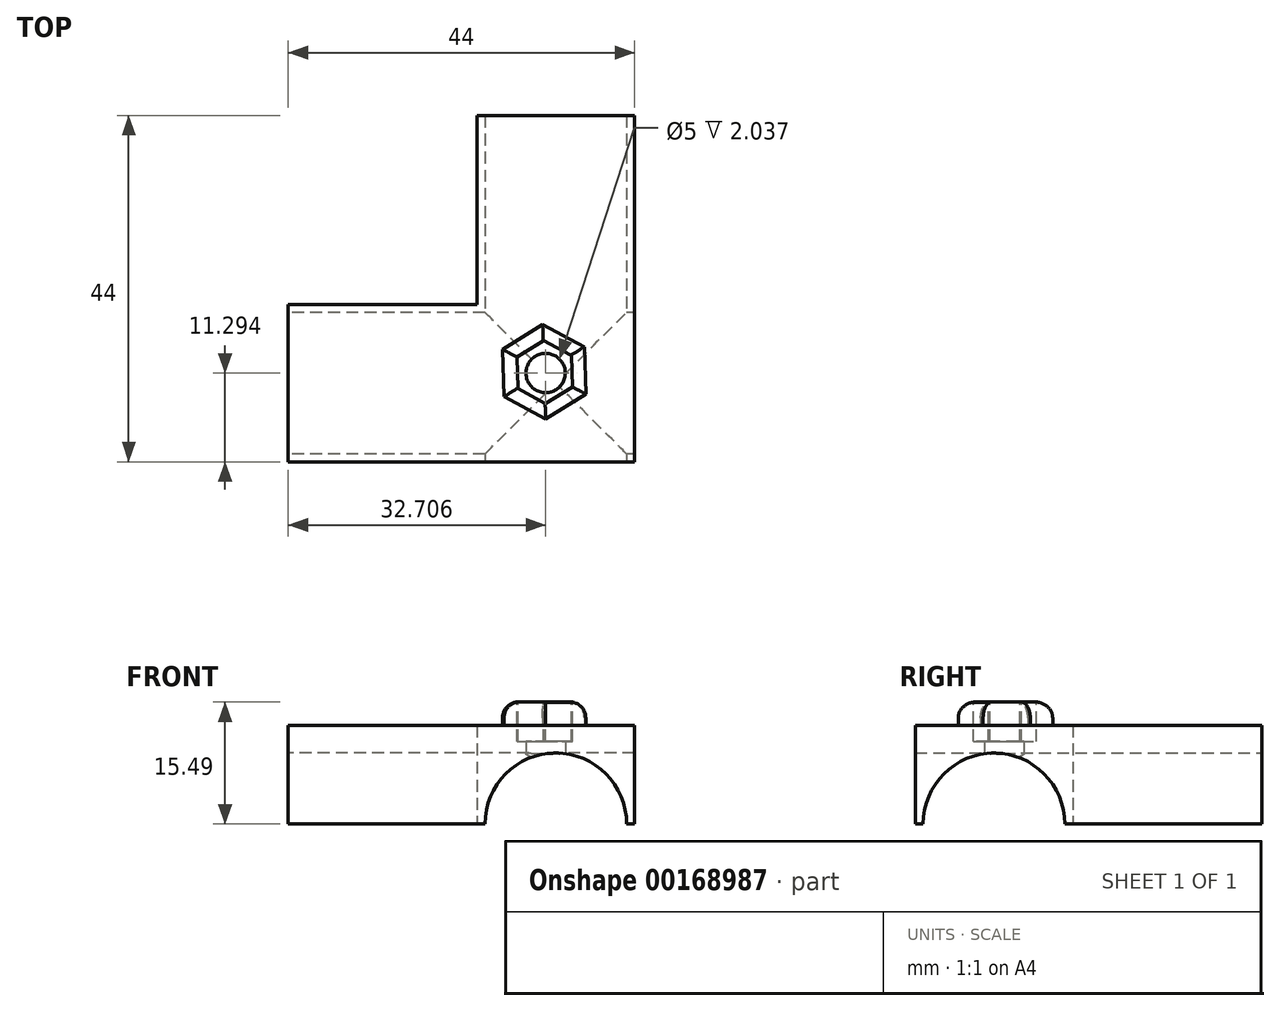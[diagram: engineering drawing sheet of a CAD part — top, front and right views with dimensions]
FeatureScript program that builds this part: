
annotation { "Feature Type Name" : "Feature", "Feature Type Description" : "" }
export const myFeature = defineFeature(function(context is Context, id is Id, definition is map)
    precondition{}
    {
        {
            var Q0;
            Q0=qCreatedBy(makeId("Top.planeOp"),FACE);
            var sketch = newSketch(context, id + "F0", { "sketchPlane" : qUnion([Q0])});
            skLineSegment(sketch, "E0", {"start": v(0, 24) * mm, "end": v(20, 24) * mm});
            skLineSegment(sketch, "E1", {"start": v(20, 24) * mm, "end": v(20, -20) * mm});
            skLineSegment(sketch, "E2", {"start": v(20, -20) * mm, "end": v(-24, -20) * mm});
            skLineSegment(sketch, "E3", {"start": v(-24, -20) * mm, "end": v(-24, 0) * mm});
            skLineSegment(sketch, "E4", {"start": v(-24, 0) * mm, "end": v(0, 0) * mm});
            skLineSegment(sketch, "E5", {"start": v(0, 0) * mm, "end": v(0, 24) * mm});
            skLineSegment(sketch, "E6", {"start": v(0, 0) * mm, "end": v(20, -20) * mm});
            skCircle(sketch, "E7", {"center": v(8.7, -8.7) * mm, "radius": 2.5 * mm});
            skSolve(sketch);
        }
        {
            var Q0;
            {var subQ4=sQuery(id+"F0.wireOp",EDGE,"E2");Q0=makeQuery(id+"F0.imprint","IMPRINT",FACE,{"disambiguationData":[TD([[makeQuery(id+"F0.imprint","IMPRINT",EDGE,{"derivedFrom":subQ4}),-1.0]])]});}
            var Q1;
            Q1=makeQuery(id+"F0.imprint","IMPRINT",FACE,{"disambiguationData":[TD([[makeQuery(id+"F0.imprint","IMPRINT",EDGE,{"derivedFrom":sQuery(id+"F0.wireOp",EDGE,"E0")}),-1.0]])]});
            extrude(context, id + "F1", {"entities" : qUnion([Q0, Q1]), "depth" : 25 * mm});
        }
        {
            var Q0;
            Q0=makeQuery(id+"F1.opExtrude","SWEPT_FACE",FACE,{"disambiguationData":[OSD([sQuery(id+"F0.wireOp",EDGE,"E3")])]});
            var sketch = newSketch(context, id + "F2", { "sketchPlane" : qUnion([Q0])});
            skCircle(sketch, "E8", {"center": v(10, 12.5) * mm, "radius": 9 * mm});
            skPoint(sketch, "E8.centerSnap0", {"position": v(0, 12.5) * mm});
            skPoint(sketch, "E9", {"position": v(10, 25) * mm});
            skSolve(sketch);
        }
        {
            var Q0;
            Q0=makeQuery(id+"F2.imprint","IMPRINT",FACE,{"disambiguationData":[TD([[makeQuery(id+"F2.imprint","IMPRINT",EDGE,{"derivedFrom":sQuery(id+"F2.wireOp",EDGE,"E8")}),1.0]])]});
            extrude(context, id + "F3", {"entities" : qUnion([Q0]), "operationType" : NewBodyOperationType.REMOVE, "endBound" : BoundingType.THROUGH_ALL, "oppositeDirection" : true, "depth" : 25 * mm});
        }
        {
            var Q0;
            Q0=makeQuery(id+"F1.opExtrude","SWEPT_FACE",FACE,{"disambiguationData":[OSD([sQuery(id+"F0.wireOp",EDGE,"E0")])]});
            var sketch = newSketch(context, id + "F4", { "sketchPlane" : qUnion([Q0])});
            skCircle(sketch, "E10", {"center": v(-10, 12.5) * mm, "radius": 9 * mm});
            skPoint(sketch, "E11", {"position": v(-10, 25) * mm});
            skPoint(sketch, "E12", {"position": v(-20, 12.5) * mm});
            skSolve(sketch);
        }
        {
            var Q0;
            Q0=makeQuery(id+"F4.imprint","IMPRINT",FACE,{"disambiguationData":[TD([[makeQuery(id+"F4.imprint","IMPRINT",EDGE,{"derivedFrom":sQuery(id+"F4.wireOp",EDGE,"E10")}),1.0]])]});
            extrude(context, id + "F5", {"entities" : qUnion([Q0]), "operationType" : NewBodyOperationType.REMOVE, "endBound" : BoundingType.THROUGH_ALL, "oppositeDirection" : true, "depth" : 25 * mm});
        }
        {
            var Q0;
            Q0=makeQuery(id+"F1.opExtrude","SWEPT_FACE",FACE,{"disambiguationData":[OSD([sQuery(id+"F0.wireOp",EDGE,"E2")])]});
            var sketch = newSketch(context, id + "F6", { "sketchPlane" : qUnion([Q0])});
            skLineSegment(sketch, "E13", {"start": v(-24, 12.5) * mm, "end": v(20, 12.5) * mm});
            skSolve(sketch);
        }
        {
            var Q0;
            {var subQ0=sQuery(id+"F0.wireOp",EDGE,"E2");var subQ1=makeQuery(id+"F1.opExtrude","CAP_EDGE",EDGE,{"disambiguationData":[OSD([subQ0])],"isStart":true});Q0=makeQuery(id+"F6.imprint","IMPRINT",FACE,{"disambiguationData":[TD([[makeQuery(id+"F6.imprint","IMPRINT",EDGE,{"derivedFrom":subQ1}),-1.0]])]});}
            extrude(context, id + "F7", {"entities" : qUnion([Q0]), "operationType" : NewBodyOperationType.REMOVE, "endBound" : BoundingType.THROUGH_ALL, "oppositeDirection" : true, "depth" : 25 * mm});
        }
        {
            var Q0;
            Q0=makeQuery(id+"F1.opExtrude","CAP_FACE",FACE,{"disambiguationData":[OSD([sQuery(id+"F0.wireOp",EDGE,"E0"),sQuery(id+"F0.wireOp",EDGE,"E1"),sQuery(id+"F0.wireOp",EDGE,"E2"),sQuery(id+"F0.wireOp",EDGE,"E3"),sQuery(id+"F0.wireOp",EDGE,"E4"),sQuery(id+"F0.wireOp",EDGE,"E5"),sQuery(id+"F0.wireOp",EDGE,"E7")])],"isStart":false});
            var sketch = newSketch(context, id + "F8", { "sketchPlane" : qUnion([Q0])});
            skCircle(sketch, "E14", {"center": v(8.7, -8.7) * mm, "radius": 2.5 * mm});
            skPoint(sketch, "E14.centerSnap0", {"position": v(8.7, 30.42) * mm});
            skLineSegment(sketch, "E15", {"start": v(5.18, -10.7) * mm, "end": v(5.06, -6.7) * mm});
            skLineSegment(sketch, "E16", {"start": v(5.06, -6.7) * mm, "end": v(8.45, -4.6) * mm});
            skLineSegment(sketch, "E17", {"start": v(5.18, -10.7) * mm, "end": v(8.7, -12.6) * mm});
            skLineSegment(sketch, "E18", {"start": v(8.7, -12.6) * mm, "end": v(12.1, -10.49) * mm});
            skLineSegment(sketch, "E19", {"start": v(12.1, -10.49) * mm, "end": v(11.98, -6.49) * mm});
            skLineSegment(sketch, "E20", {"start": v(11.98, -6.49) * mm, "end": v(8.45, -4.6) * mm});
            skPoint(sketch, "E21", {"position": v(5.12, -8.7) * mm});
            skLineSegment(sketch, "E22", {"start": v(3.42, -11.7) * mm, "end": v(3.23, -5.7) * mm});
            skLineSegment(sketch, "E23", {"start": v(3.23, -5.7) * mm, "end": v(8.33, -2.55) * mm});
            skLineSegment(sketch, "E24", {"start": v(3.42, -11.7) * mm, "end": v(8.7, -14.54) * mm});
            skLineSegment(sketch, "E25", {"start": v(8.7, -14.54) * mm, "end": v(13.8, -11.38) * mm});
            skLineSegment(sketch, "E26", {"start": v(13.8, -11.38) * mm, "end": v(13.62, -5.38) * mm});
            skLineSegment(sketch, "E27", {"start": v(13.62, -5.38) * mm, "end": v(8.33, -2.55) * mm});
            skPoint(sketch, "E28", {"position": v(3.32, -8.7) * mm});
            skSolve(sketch);
        }
        {
            var Q0;
            Q0=makeQuery(id+"F8.imprint","IMPRINT",FACE,{"disambiguationData":[TD([[makeQuery(id+"F8.imprint","IMPRINT",EDGE,{"derivedFrom":sQuery(id+"F8.wireOp",EDGE,"E14")}),-1.0]])]});
            extrude(context, id + "F9", {"entities" : qUnion([Q0]), "operationType" : NewBodyOperationType.REMOVE, "oppositeDirection" : true, "depth" : 2 * mm});
        }
        {
            var Q0;
            Q0=makeQuery(id+"F8.imprint","IMPRINT",FACE,{"disambiguationData":[TD([[makeQuery(id+"F8.imprint","IMPRINT",EDGE,{"derivedFrom":sQuery(id+"F8.wireOp",EDGE,"E15")}),1.0]])]});
            extrude(context, id + "F10", {"entities" : qUnion([Q0]), "operationType" : NewBodyOperationType.ADD, "depth" : 3 * mm});
        }
        {
            var Q0;
            Q0=makeQuery(id+"F10.opExtrude","CAP_EDGE",EDGE,{"disambiguationData":[OSD([sQuery(id+"F8.wireOp",EDGE,"E27")])],"isStart":false});
            var Q1;
            Q1=makeQuery(id+"F10.opExtrude","CAP_EDGE",EDGE,{"disambiguationData":[OSD([sQuery(id+"F8.wireOp",EDGE,"E26")])],"isStart":false});
            var Q2;
            Q2=makeQuery(id+"F10.opExtrude","CAP_EDGE",EDGE,{"disambiguationData":[OSD([sQuery(id+"F8.wireOp",EDGE,"E25")])],"isStart":false});
            var Q3;
            Q3=makeQuery(id+"F10.opExtrude","CAP_EDGE",EDGE,{"disambiguationData":[OSD([sQuery(id+"F8.wireOp",EDGE,"E24")])],"isStart":false});
            var Q4;
            Q4=makeQuery(id+"F10.opExtrude","CAP_EDGE",EDGE,{"disambiguationData":[OSD([sQuery(id+"F8.wireOp",EDGE,"E22")])],"isStart":false});
            var Q5;
            Q5=makeQuery(id+"F10.opExtrude","CAP_EDGE",EDGE,{"disambiguationData":[OSD([sQuery(id+"F8.wireOp",EDGE,"E23")])],"isStart":false});
            fillet(context, id + "F11", {"entities" : qUnion([Q0, Q1, Q2, Q3, Q4, Q5]), "radius" : 2 * mm, "tangentPropagation" : true, "allowEdgeOverflow" : false});
        }
    });
